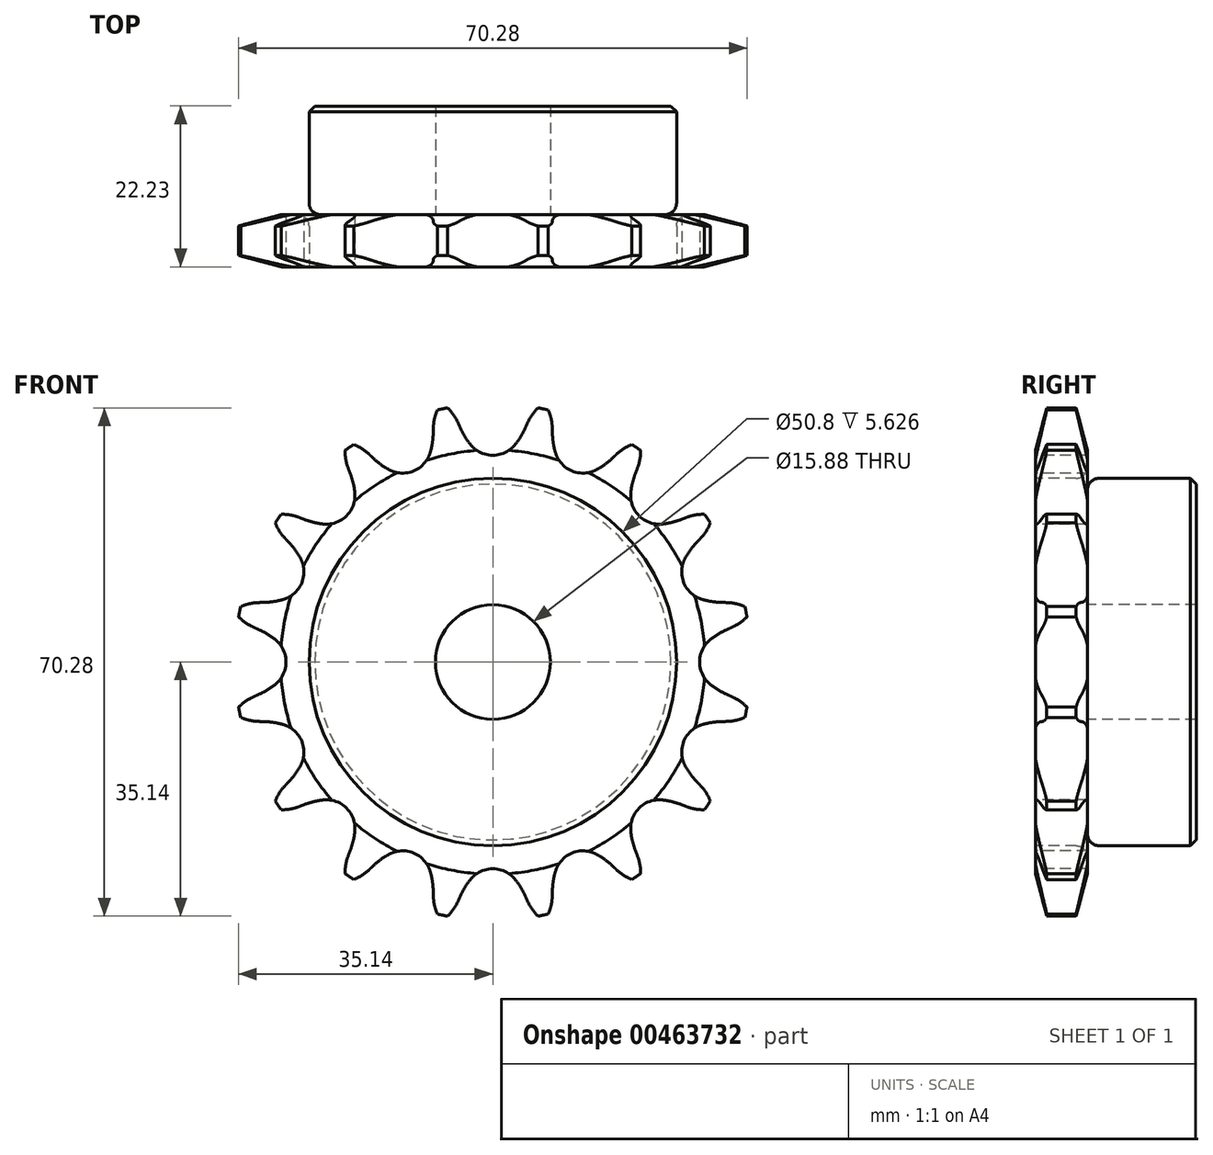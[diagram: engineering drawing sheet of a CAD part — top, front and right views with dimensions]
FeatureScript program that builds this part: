
annotation { "Feature Type Name" : "Feature", "Feature Type Description" : "" }
export const myFeature = defineFeature(function(context is Context, id is Id, definition is map)
    precondition{}
    {
        {
            var Q0;
            Q0=qCreatedBy(makeId("Right.planeOp"),FACE);
            var sketch = newSketch(context, id + "F0", { "sketchPlane" : qUnion([Q0])});
            skLineSegment(sketch, "E0", {"start": v(0, 0) * mm, "end": v(22.23, 0) * mm, "construction": true});
            skLineSegment(sketch, "E1.bottom", {"start": v(0, 7.94) * mm, "end": v(7.21, 7.94) * mm});
            skLineSegment(sketch, "E1.top", {"start": v(0, 35.69) * mm, "end": v(7.21, 35.69) * mm});
            skLineSegment(sketch, "E1.left", {"start": v(0, 7.94) * mm, "end": v(0, 35.69) * mm});
            skLineSegment(sketch, "E1.right", {"start": v(7.21, 7.94) * mm, "end": v(7.21, 35.69) * mm});
            skLineSegment(sketch, "E2.bottom", {"start": v(0, 7.94) * mm, "end": v(22.23, 7.94) * mm});
            skLineSegment(sketch, "E2.top", {"start": v(0, 25.4) * mm, "end": v(22.22, 25.4) * mm});
            skLineSegment(sketch, "E2.left", {"start": v(0, 7.94) * mm, "end": v(0, 25.4) * mm});
            skLineSegment(sketch, "E2.right", {"start": v(22.23, 7.94) * mm, "end": v(22.22, 25.4) * mm});
            skLineSegment(sketch, "E3.MirrorCS", {"start": v(0, -7.94) * mm, "end": v(7.21, -7.94) * mm});
            skLineSegment(sketch, "E4.MirrorCS", {"start": v(22.23, -7.94) * mm, "end": v(22.23, -25.4) * mm});
            skLineSegment(sketch, "E5.MirrorCS", {"start": v(0, -7.94) * mm, "end": v(0, -25.4) * mm});
            skLineSegment(sketch, "E6.MirrorCS", {"start": v(0, -35.69) * mm, "end": v(7.21, -35.69) * mm});
            skLineSegment(sketch, "E7.MirrorCS", {"start": v(0, -7.94) * mm, "end": v(0, -35.69) * mm});
            skLineSegment(sketch, "E8.MirrorCS", {"start": v(7.21, -7.94) * mm, "end": v(7.21, -35.69) * mm});
            skLineSegment(sketch, "E9.MirrorCS", {"start": v(0, -25.4) * mm, "end": v(22.22, -25.4) * mm});
            skLineSegment(sketch, "E10.MirrorCS", {"start": v(0, -7.94) * mm, "end": v(22.23, -7.94) * mm});
            skSolve(sketch);
        }
        {
            var Q0;
            {var subQ5=sQuery(id+"F0.wireOp",EDGE,"E2.left");Q0=makeQuery(id+"F0.imprint","IMPRINT",FACE,{"disambiguationData":[TD([[makeQuery(id+"F0.imprint","IMPRINT",EDGE,{"derivedFrom":subQ5}),-1.0]])]});}
            var Q1;
            {var subQ0=sQuery(id+"F0.wireOp",EDGE,"E1.top");Q1=makeQuery(id+"F0.imprint","IMPRINT",FACE,{"disambiguationData":[TD([[makeQuery(id+"F0.imprint","IMPRINT",EDGE,{"derivedFrom":subQ0}),-1.0]])]});}
            var Q2;
            {var subQ5=sQuery(id+"F0.wireOp",EDGE,"E2.right");Q2=makeQuery(id+"F0.imprint","IMPRINT",FACE,{"disambiguationData":[TD([[makeQuery(id+"F0.imprint","IMPRINT",EDGE,{"derivedFrom":subQ5}),1.0]])]});}
            var Q3;
            Q3=sQuery(id+"F0.wireOp",EDGE,"E0");
            revolve(context, id + "F1", {"entities" : qUnion([Q0, Q1, Q2]), "axis" : qUnion([Q3]), "revolveType" : RevolveType.FULL});
        }
        {
            var Q0;
            Q0=makeQuery(id+"F1.opRevolve","SWEPT_EDGE",EDGE,{"disambiguationData":[OSD([sQuery(id+"F0.wireOp",EDGE,"E1.right"),sQuery(id+"F0.wireOp",EDGE,"E2.top")])]});
            fillet(context, id + "F2", {"entities" : qUnion([Q0]), "radius" : 1.59 * mm, "tangentPropagation" : true, "allowEdgeOverflow" : false});
        }
        {
            var Q0;
            Q0=makeQuery(id+"F1.opRevolve","SWEPT_EDGE",EDGE,{"disambiguationData":[OSD([sQuery(id+"F0.wireOp",EDGE,"E2.top"),sQuery(id+"F0.wireOp",EDGE,"E2.right")])]});
            chamfer(context, id + "F3", {"entities" : qUnion([Q0]), "width" : 0.8 * mm, "tangentPropagation" : true});
        }
        {
            var Q0;
            Q0=makeQuery(id+"F1.opRevolve","SWEPT_EDGE",EDGE,{"disambiguationData":[OSD([sQuery(id+"F0.wireOp",EDGE,"E1.top"),sQuery(id+"F0.wireOp",EDGE,"E1.right")])]});
            var Q1;
            Q1=makeQuery(id+"F1.opRevolve","SWEPT_EDGE",EDGE,{"disambiguationData":[OSD([sQuery(id+"F0.wireOp",EDGE,"E1.top"),sQuery(id+"F0.wireOp",EDGE,"E1.left")])]});
            chamfer(context, id + "F4", {"entities" : qUnion([Q0, Q1]), "chamferType" : ChamferType.TWO_OFFSETS, "width1" : 6.35 * mm, "oppositeDirection" : true, "width2" : 1.57 * mm, "tangentPropagation" : true});
        }
        {
            var Q0;
            Q0=makeQuery(id+"F1.opRevolve","SWEPT_FACE",FACE,{"disambiguationData":[OSD([sQuery(id+"F0.wireOp",EDGE,"E1.left"),sQuery(id+"F0.wireOp",EDGE,"E2.left")])]});
            var sketch = newSketch(context, id + "F5", { "sketchPlane" : qUnion([Q0])});
            skCircle(sketch, "E11", {"center": v(0, 0) * mm, "radius": 32.55 * mm, "construction": true});
            skLineSegment(sketch, "E12", {"start": v(0, 0) * mm, "end": v(0, 32.55) * mm, "construction": true});
            skLineSegment(sketch, "E13", {"start": v(0, 32.55) * mm, "end": v(46.31, 32.55) * mm, "construction": true});
            skLineSegment(sketch, "E14", {"start": v(0, 32.55) * mm, "end": v(5, 36.56) * mm, "construction": true});
            skLineSegment(sketch, "E15", {"start": v(5, 36.56) * mm, "end": v(-4.46, 32.3) * mm, "construction": true});
            skLineSegment(sketch, "E16", {"start": v(-4.46, 32.3) * mm, "end": v(-4.82, 33.1) * mm});
            skLineSegment(sketch, "E17", {"start": v(0, 0) * mm, "end": v(-7.13, 35.85) * mm, "construction": true});
            skLineSegment(sketch, "E18", {"start": v(-7.13, 35.85) * mm, "end": v(-7.13, 35.85) * mm});
            skArc(sketch, "E19", {"start": v(-4.82, 33.1) * mm, "mid": v(-5.78, 34.63) * mm, "end": v(-7.13, 35.85) * mm});
            skArc(sketch, "E20", {"start": v(-7.13, 35.85) * mm, "mid": v(-15.87, 26.15) * mm, "end": v(-4.82, 33.1) * mm, "construction": true});
            skArc(sketch, "E21", {"start": v(-4.46, 32.3) * mm, "mid": v(-3.84, 31.14) * mm, "end": v(-3.1, 30.07) * mm});
            skArc(sketch, "E22", {"start": v(-3.1, 30.07) * mm, "mid": v(13.83, 41.97) * mm, "end": v(-4.46, 32.3) * mm, "construction": true});
            skArc(sketch, "E23.MirrorCS", {"start": v(4.46, 32.3) * mm, "mid": v(3.84, 31.14) * mm, "end": v(3.1, 30.07) * mm});
            skLineSegment(sketch, "E24.MirrorCS", {"start": v(4.46, 32.3) * mm, "end": v(4.82, 33.1) * mm});
            skArc(sketch, "E25.MirrorCS", {"start": v(4.82, 33.1) * mm, "mid": v(5.78, 34.63) * mm, "end": v(7.13, 35.85) * mm});
            skArc(sketch, "E26", {"start": v(-3.1, 30.07) * mm, "mid": v(0, 28.59) * mm, "end": v(3.1, 30.07) * mm});
            skArc(sketch, "E27", {"start": v(3.1, 30.07) * mm, "mid": v(0, 36.51) * mm, "end": v(-3.1, 30.07) * mm, "construction": true});
            skArc(sketch, "E28.1.0", {"start": v(-17.12, 28.74) * mm, "mid": v(-18.6, 29.79) * mm, "end": v(-20.3, 30.4) * mm});
            skLineSegment(sketch, "E28.1.1", {"start": v(-16.48, 28.14) * mm, "end": v(-17.12, 28.74) * mm});
            skArc(sketch, "E28.1.2", {"start": v(-16.48, 28.14) * mm, "mid": v(-15.47, 27.3) * mm, "end": v(-14.36, 26.6) * mm});
            skArc(sketch, "E28.1.3", {"start": v(-14.36, 26.6) * mm, "mid": v(-10.94, 26.41) * mm, "end": v(-8.65, 28.96) * mm});
            skArc(sketch, "E28.1.4", {"start": v(-8.24, 31.55) * mm, "mid": v(-8.37, 30.24) * mm, "end": v(-8.65, 28.96) * mm});
            skLineSegment(sketch, "E28.1.5", {"start": v(-8.24, 31.55) * mm, "end": v(-8.22, 32.42) * mm});
            skArc(sketch, "E28.1.6", {"start": v(-8.22, 32.42) * mm, "mid": v(-7.91, 34.21) * mm, "end": v(-7.13, 35.85) * mm});
            skArc(sketch, "E28.2.0", {"start": v(-26.8, 20) * mm, "mid": v(-28.58, 20.4) * mm, "end": v(-30.4, 20.3) * mm});
            skLineSegment(sketch, "E28.2.1", {"start": v(-26, 19.69) * mm, "end": v(-26.8, 20) * mm});
            skArc(sketch, "E28.2.2", {"start": v(-26, 19.69) * mm, "mid": v(-24.74, 19.3) * mm, "end": v(-23.45, 19.08) * mm});
            skArc(sketch, "E28.2.3", {"start": v(-23.45, 19.08) * mm, "mid": v(-20.21, 20.21) * mm, "end": v(-19.08, 23.45) * mm});
            skArc(sketch, "E28.2.4", {"start": v(-19.69, 26) * mm, "mid": v(-19.3, 24.74) * mm, "end": v(-19.08, 23.45) * mm});
            skLineSegment(sketch, "E28.2.5", {"start": v(-19.69, 26) * mm, "end": v(-20, 26.8) * mm});
            skArc(sketch, "E28.2.6", {"start": v(-20, 26.8) * mm, "mid": v(-20.4, 28.58) * mm, "end": v(-20.3, 30.4) * mm});
            skArc(sketch, "E29.1.3.0", {"start": v(-32.42, 8.22) * mm, "mid": v(-34.21, 7.91) * mm, "end": v(-35.85, 7.13) * mm});
            skLineSegment(sketch, "E29.4.3.0", {"start": v(-31.55, 8.24) * mm, "end": v(-32.42, 8.22) * mm});
            skArc(sketch, "E29.7.3.0", {"start": v(-31.55, 8.24) * mm, "mid": v(-30.24, 8.37) * mm, "end": v(-28.96, 8.65) * mm});
            skArc(sketch, "E29.11.3.0", {"start": v(-28.96, 8.65) * mm, "mid": v(-26.41, 10.94) * mm, "end": v(-26.6, 14.36) * mm});
            skArc(sketch, "E29.15.3.0", {"start": v(-28.14, 16.48) * mm, "mid": v(-27.3, 15.47) * mm, "end": v(-26.6, 14.36) * mm});
            skLineSegment(sketch, "E29.19.3.0", {"start": v(-28.14, 16.48) * mm, "end": v(-28.74, 17.12) * mm});
            skArc(sketch, "E29.22.3.0", {"start": v(-28.74, 17.12) * mm, "mid": v(-29.79, 18.6) * mm, "end": v(-30.4, 20.3) * mm});
            skArc(sketch, "E29.1.4.0", {"start": v(-33.1, -4.82) * mm, "mid": v(-34.63, -5.78) * mm, "end": v(-35.85, -7.13) * mm});
            skLineSegment(sketch, "E29.4.4.0", {"start": v(-32.3, -4.46) * mm, "end": v(-33.1, -4.82) * mm});
            skArc(sketch, "E29.7.4.0", {"start": v(-32.3, -4.46) * mm, "mid": v(-31.14, -3.84) * mm, "end": v(-30.07, -3.1) * mm});
            skArc(sketch, "E29.11.4.0", {"start": v(-30.07, -3.1) * mm, "mid": v(-28.59, 0) * mm, "end": v(-30.07, 3.1) * mm});
            skArc(sketch, "E29.15.4.0", {"start": v(-32.3, 4.46) * mm, "mid": v(-31.14, 3.84) * mm, "end": v(-30.07, 3.1) * mm});
            skLineSegment(sketch, "E29.19.4.0", {"start": v(-32.3, 4.46) * mm, "end": v(-33.1, 4.82) * mm});
            skArc(sketch, "E29.22.4.0", {"start": v(-33.1, 4.82) * mm, "mid": v(-34.63, 5.78) * mm, "end": v(-35.85, 7.13) * mm});
            skArc(sketch, "E29.1.5.0", {"start": v(-28.74, -17.12) * mm, "mid": v(-29.79, -18.6) * mm, "end": v(-30.4, -20.3) * mm});
            skLineSegment(sketch, "E29.4.5.0", {"start": v(-28.14, -16.48) * mm, "end": v(-28.74, -17.12) * mm});
            skArc(sketch, "E29.7.5.0", {"start": v(-28.14, -16.48) * mm, "mid": v(-27.3, -15.47) * mm, "end": v(-26.6, -14.36) * mm});
            skArc(sketch, "E29.11.5.0", {"start": v(-26.6, -14.36) * mm, "mid": v(-26.41, -10.94) * mm, "end": v(-28.96, -8.65) * mm});
            skArc(sketch, "E29.15.5.0", {"start": v(-31.55, -8.24) * mm, "mid": v(-30.24, -8.37) * mm, "end": v(-28.96, -8.65) * mm});
            skLineSegment(sketch, "E29.19.5.0", {"start": v(-31.55, -8.24) * mm, "end": v(-32.42, -8.22) * mm});
            skArc(sketch, "E29.22.5.0", {"start": v(-32.42, -8.22) * mm, "mid": v(-34.21, -7.91) * mm, "end": v(-35.85, -7.13) * mm});
            skArc(sketch, "E29.1.6.0", {"start": v(-20, -26.8) * mm, "mid": v(-20.4, -28.58) * mm, "end": v(-20.3, -30.4) * mm});
            skLineSegment(sketch, "E29.4.6.0", {"start": v(-19.69, -26) * mm, "end": v(-20, -26.8) * mm});
            skArc(sketch, "E29.7.6.0", {"start": v(-19.69, -26) * mm, "mid": v(-19.3, -24.74) * mm, "end": v(-19.08, -23.45) * mm});
            skArc(sketch, "E29.11.6.0", {"start": v(-19.08, -23.45) * mm, "mid": v(-20.21, -20.21) * mm, "end": v(-23.45, -19.08) * mm});
            skArc(sketch, "E29.15.6.0", {"start": v(-26, -19.69) * mm, "mid": v(-24.74, -19.3) * mm, "end": v(-23.45, -19.08) * mm});
            skLineSegment(sketch, "E29.19.6.0", {"start": v(-26, -19.69) * mm, "end": v(-26.8, -20) * mm});
            skArc(sketch, "E29.22.6.0", {"start": v(-26.8, -20) * mm, "mid": v(-28.58, -20.4) * mm, "end": v(-30.4, -20.3) * mm});
            skArc(sketch, "E29.1.7.0", {"start": v(-8.22, -32.42) * mm, "mid": v(-7.91, -34.21) * mm, "end": v(-7.13, -35.85) * mm});
            skLineSegment(sketch, "E29.4.7.0", {"start": v(-8.24, -31.55) * mm, "end": v(-8.22, -32.42) * mm});
            skArc(sketch, "E29.7.7.0", {"start": v(-8.24, -31.55) * mm, "mid": v(-8.37, -30.24) * mm, "end": v(-8.65, -28.96) * mm});
            skArc(sketch, "E29.11.7.0", {"start": v(-8.65, -28.96) * mm, "mid": v(-10.94, -26.41) * mm, "end": v(-14.36, -26.6) * mm});
            skArc(sketch, "E29.15.7.0", {"start": v(-16.48, -28.14) * mm, "mid": v(-15.47, -27.3) * mm, "end": v(-14.36, -26.6) * mm});
            skLineSegment(sketch, "E29.19.7.0", {"start": v(-16.48, -28.14) * mm, "end": v(-17.12, -28.74) * mm});
            skArc(sketch, "E29.22.7.0", {"start": v(-17.12, -28.74) * mm, "mid": v(-18.6, -29.79) * mm, "end": v(-20.3, -30.4) * mm});
            skArc(sketch, "E29.1.8.0", {"start": v(4.82, -33.1) * mm, "mid": v(5.78, -34.63) * mm, "end": v(7.13, -35.85) * mm});
            skLineSegment(sketch, "E29.4.8.0", {"start": v(4.46, -32.3) * mm, "end": v(4.82, -33.1) * mm});
            skArc(sketch, "E29.7.8.0", {"start": v(4.46, -32.3) * mm, "mid": v(3.84, -31.14) * mm, "end": v(3.1, -30.07) * mm});
            skArc(sketch, "E29.11.8.0", {"start": v(3.1, -30.07) * mm, "mid": v(0, -28.59) * mm, "end": v(-3.1, -30.07) * mm});
            skArc(sketch, "E29.15.8.0", {"start": v(-4.46, -32.3) * mm, "mid": v(-3.84, -31.14) * mm, "end": v(-3.1, -30.07) * mm});
            skLineSegment(sketch, "E29.19.8.0", {"start": v(-4.46, -32.3) * mm, "end": v(-4.82, -33.1) * mm});
            skArc(sketch, "E29.22.8.0", {"start": v(-4.82, -33.1) * mm, "mid": v(-5.78, -34.63) * mm, "end": v(-7.13, -35.85) * mm});
            skArc(sketch, "E29.1.9.0", {"start": v(17.12, -28.74) * mm, "mid": v(18.6, -29.79) * mm, "end": v(20.3, -30.4) * mm});
            skLineSegment(sketch, "E29.4.9.0", {"start": v(16.48, -28.14) * mm, "end": v(17.12, -28.74) * mm});
            skArc(sketch, "E29.7.9.0", {"start": v(16.48, -28.14) * mm, "mid": v(15.47, -27.3) * mm, "end": v(14.36, -26.6) * mm});
            skArc(sketch, "E29.11.9.0", {"start": v(14.36, -26.6) * mm, "mid": v(10.94, -26.41) * mm, "end": v(8.65, -28.96) * mm});
            skArc(sketch, "E29.15.9.0", {"start": v(8.24, -31.55) * mm, "mid": v(8.37, -30.24) * mm, "end": v(8.65, -28.96) * mm});
            skLineSegment(sketch, "E29.19.9.0", {"start": v(8.24, -31.55) * mm, "end": v(8.22, -32.42) * mm});
            skArc(sketch, "E29.22.9.0", {"start": v(8.22, -32.42) * mm, "mid": v(7.91, -34.21) * mm, "end": v(7.13, -35.85) * mm});
            skArc(sketch, "E29.1.10.0", {"start": v(26.8, -20) * mm, "mid": v(28.58, -20.4) * mm, "end": v(30.4, -20.3) * mm});
            skLineSegment(sketch, "E29.4.10.0", {"start": v(26, -19.69) * mm, "end": v(26.8, -20) * mm});
            skArc(sketch, "E29.7.10.0", {"start": v(26, -19.69) * mm, "mid": v(24.74, -19.3) * mm, "end": v(23.45, -19.08) * mm});
            skArc(sketch, "E29.11.10.0", {"start": v(23.45, -19.08) * mm, "mid": v(20.21, -20.21) * mm, "end": v(19.08, -23.45) * mm});
            skArc(sketch, "E29.15.10.0", {"start": v(19.69, -26) * mm, "mid": v(19.3, -24.74) * mm, "end": v(19.08, -23.45) * mm});
            skLineSegment(sketch, "E29.19.10.0", {"start": v(19.69, -26) * mm, "end": v(20, -26.8) * mm});
            skArc(sketch, "E29.22.10.0", {"start": v(20, -26.8) * mm, "mid": v(20.4, -28.58) * mm, "end": v(20.3, -30.4) * mm});
            skArc(sketch, "E29.1.11.0", {"start": v(32.42, -8.22) * mm, "mid": v(34.21, -7.91) * mm, "end": v(35.85, -7.13) * mm});
            skLineSegment(sketch, "E29.4.11.0", {"start": v(31.55, -8.24) * mm, "end": v(32.42, -8.22) * mm});
            skArc(sketch, "E29.7.11.0", {"start": v(31.55, -8.24) * mm, "mid": v(30.24, -8.37) * mm, "end": v(28.96, -8.65) * mm});
            skArc(sketch, "E29.11.11.0", {"start": v(28.96, -8.65) * mm, "mid": v(26.41, -10.94) * mm, "end": v(26.6, -14.36) * mm});
            skArc(sketch, "E29.15.11.0", {"start": v(28.14, -16.48) * mm, "mid": v(27.3, -15.47) * mm, "end": v(26.6, -14.36) * mm});
            skLineSegment(sketch, "E29.19.11.0", {"start": v(28.14, -16.48) * mm, "end": v(28.74, -17.12) * mm});
            skArc(sketch, "E29.22.11.0", {"start": v(28.74, -17.12) * mm, "mid": v(29.79, -18.6) * mm, "end": v(30.4, -20.3) * mm});
            skArc(sketch, "E29.1.12.0", {"start": v(33.1, 4.82) * mm, "mid": v(34.63, 5.78) * mm, "end": v(35.85, 7.13) * mm});
            skLineSegment(sketch, "E29.4.12.0", {"start": v(32.3, 4.46) * mm, "end": v(33.1, 4.82) * mm});
            skArc(sketch, "E29.7.12.0", {"start": v(32.3, 4.46) * mm, "mid": v(31.14, 3.84) * mm, "end": v(30.07, 3.1) * mm});
            skArc(sketch, "E29.11.12.0", {"start": v(30.07, 3.1) * mm, "mid": v(28.59, 0) * mm, "end": v(30.07, -3.1) * mm});
            skArc(sketch, "E29.15.12.0", {"start": v(32.3, -4.46) * mm, "mid": v(31.14, -3.84) * mm, "end": v(30.07, -3.1) * mm});
            skLineSegment(sketch, "E29.19.12.0", {"start": v(32.3, -4.46) * mm, "end": v(33.1, -4.82) * mm});
            skArc(sketch, "E29.22.12.0", {"start": v(33.1, -4.82) * mm, "mid": v(34.63, -5.78) * mm, "end": v(35.85, -7.13) * mm});
            skArc(sketch, "E29.1.13.0", {"start": v(28.74, 17.12) * mm, "mid": v(29.79, 18.6) * mm, "end": v(30.4, 20.3) * mm});
            skLineSegment(sketch, "E29.4.13.0", {"start": v(28.14, 16.48) * mm, "end": v(28.74, 17.12) * mm});
            skArc(sketch, "E29.7.13.0", {"start": v(28.14, 16.48) * mm, "mid": v(27.3, 15.47) * mm, "end": v(26.6, 14.36) * mm});
            skArc(sketch, "E29.11.13.0", {"start": v(26.6, 14.36) * mm, "mid": v(26.41, 10.94) * mm, "end": v(28.96, 8.65) * mm});
            skArc(sketch, "E29.15.13.0", {"start": v(31.55, 8.24) * mm, "mid": v(30.24, 8.37) * mm, "end": v(28.96, 8.65) * mm});
            skLineSegment(sketch, "E29.19.13.0", {"start": v(31.55, 8.24) * mm, "end": v(32.42, 8.22) * mm});
            skArc(sketch, "E29.22.13.0", {"start": v(32.42, 8.22) * mm, "mid": v(34.21, 7.91) * mm, "end": v(35.85, 7.13) * mm});
            skArc(sketch, "E29.1.14.0", {"start": v(20, 26.8) * mm, "mid": v(20.4, 28.58) * mm, "end": v(20.3, 30.4) * mm});
            skLineSegment(sketch, "E29.4.14.0", {"start": v(19.69, 26) * mm, "end": v(20, 26.8) * mm});
            skArc(sketch, "E29.7.14.0", {"start": v(19.69, 26) * mm, "mid": v(19.3, 24.74) * mm, "end": v(19.08, 23.45) * mm});
            skArc(sketch, "E29.11.14.0", {"start": v(19.08, 23.45) * mm, "mid": v(20.21, 20.21) * mm, "end": v(23.45, 19.08) * mm});
            skArc(sketch, "E29.15.14.0", {"start": v(26, 19.69) * mm, "mid": v(24.74, 19.3) * mm, "end": v(23.45, 19.08) * mm});
            skLineSegment(sketch, "E29.19.14.0", {"start": v(26, 19.69) * mm, "end": v(26.8, 20) * mm});
            skArc(sketch, "E29.22.14.0", {"start": v(26.8, 20) * mm, "mid": v(28.58, 20.4) * mm, "end": v(30.4, 20.3) * mm});
            skArc(sketch, "E29.1.15.0", {"start": v(8.22, 32.42) * mm, "mid": v(7.91, 34.21) * mm, "end": v(7.13, 35.85) * mm});
            skLineSegment(sketch, "E29.4.15.0", {"start": v(8.24, 31.55) * mm, "end": v(8.22, 32.42) * mm});
            skArc(sketch, "E29.7.15.0", {"start": v(8.24, 31.55) * mm, "mid": v(8.37, 30.24) * mm, "end": v(8.65, 28.96) * mm});
            skArc(sketch, "E29.11.15.0", {"start": v(8.65, 28.96) * mm, "mid": v(10.94, 26.41) * mm, "end": v(14.36, 26.6) * mm});
            skArc(sketch, "E29.15.15.0", {"start": v(16.48, 28.14) * mm, "mid": v(15.47, 27.3) * mm, "end": v(14.36, 26.6) * mm});
            skLineSegment(sketch, "E29.19.15.0", {"start": v(16.48, 28.14) * mm, "end": v(17.12, 28.74) * mm});
            skArc(sketch, "E29.22.15.0", {"start": v(17.12, 28.74) * mm, "mid": v(18.6, 29.79) * mm, "end": v(20.3, 30.4) * mm});
            skSolve(sketch);
        }
        {
            var Q0;
            Q0 = qSketchRegion(id + "F5", true);
            extrude(context, id + "F6", {"entities" : qUnion([Q0]), "operationType" : NewBodyOperationType.INTERSECT, "endBound" : BoundingType.THROUGH_ALL, "oppositeDirection" : true, "depth" : 25.4 * mm});
        }
    });
